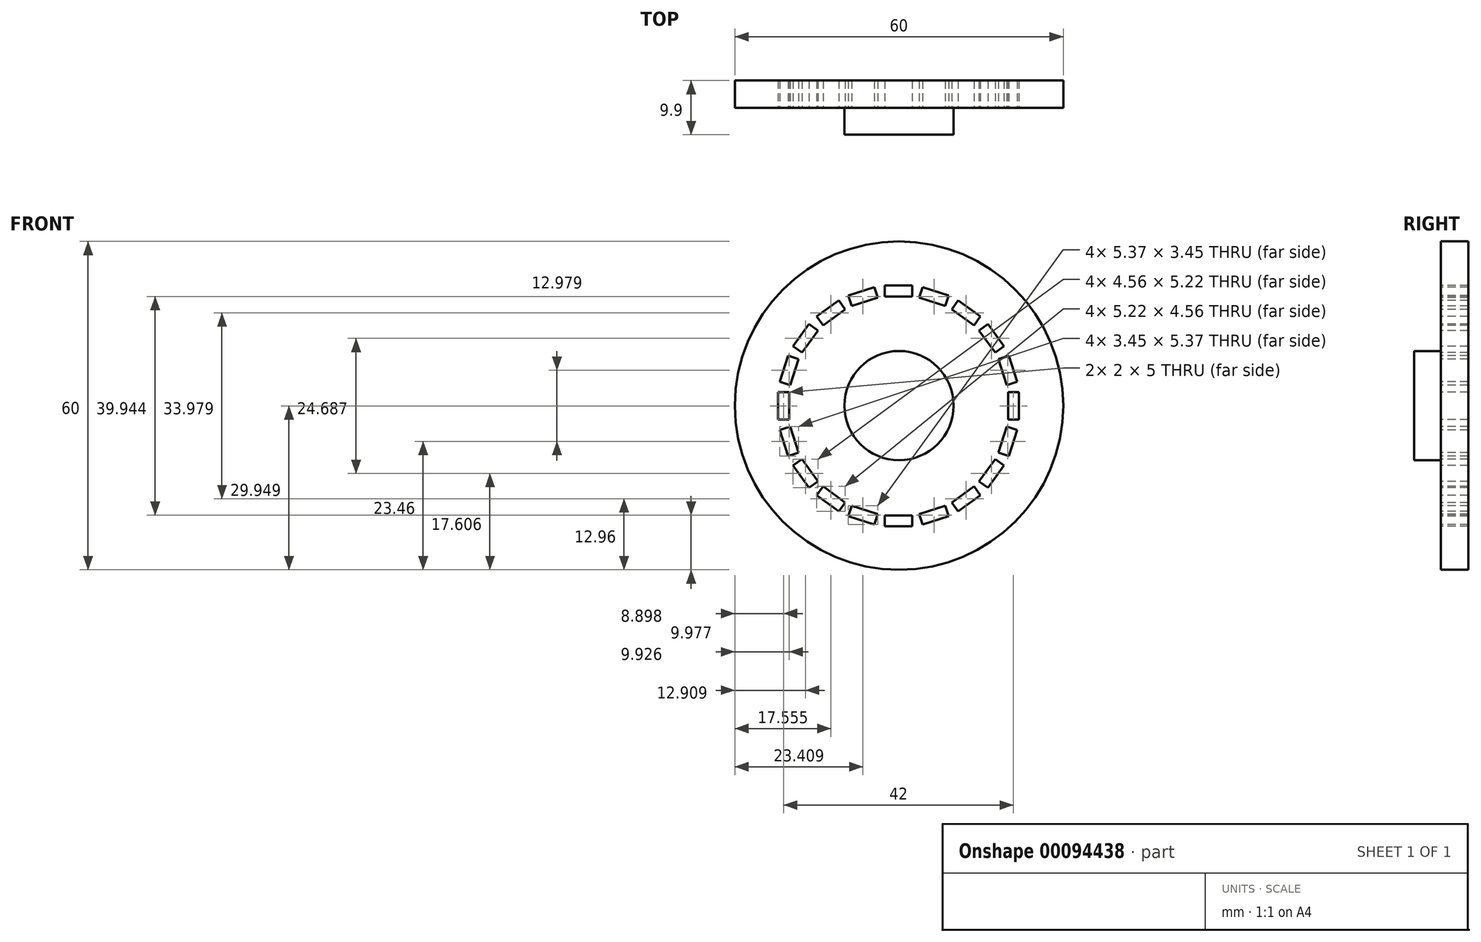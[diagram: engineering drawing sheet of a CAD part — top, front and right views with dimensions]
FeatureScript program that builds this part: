
annotation { "Feature Type Name" : "Feature", "Feature Type Description" : "" }
export const myFeature = defineFeature(function(context is Context, id is Id, definition is map)
    precondition{}
    {
        {
            var Q0;
            Q0=qCreatedBy(makeId("Front.planeOp"),FACE);
            var sketch = newSketch(context, id + "F0", { "sketchPlane" : qUnion([Q0])});
            skCircle(sketch, "E0", {"center": v(0, 0) * mm, "radius": 30 * mm});
            skSolve(sketch);
        }
        {
            var Q0;
            Q0=makeQuery(id+"F0.imprint","IMPRINT",FACE,{"disambiguationData":[TD([[makeQuery(id+"F0.imprint","IMPRINT",EDGE,{"derivedFrom":sQuery(id+"F0.wireOp",EDGE,"E0")}),1.0]])]});
            extrude(context, id + "F1", {"entities" : qUnion([Q0]), "depth" : 5 * mm});
        }
        {
            var Q0;
            Q0=makeQuery(id+"F1.opExtrude","CAP_FACE",FACE,{"disambiguationData":[OSD([sQuery(id+"F0.wireOp",EDGE,"E0")])],"isStart":false});
            var sketch = newSketch(context, id + "F2", { "sketchPlane" : qUnion([Q0])});
            skLineSegment(sketch, "E1", {"start": v(-2.6, 20.95) * mm, "end": v(-2.6, 21.95) * mm});
            skLineSegment(sketch, "E2", {"start": v(-2.6, 21.95) * mm, "end": v(2.4, 21.95) * mm});
            skLineSegment(sketch, "E3", {"start": v(2.4, 21.95) * mm, "end": v(2.4, 19.95) * mm});
            skLineSegment(sketch, "E4", {"start": v(2.4, 19.95) * mm, "end": v(-2.6, 19.95) * mm});
            skLineSegment(sketch, "E5", {"start": v(-2.6, 19.95) * mm, "end": v(-2.6, 20.95) * mm});
            skLineSegment(sketch, "E6.1.0", {"start": v(-9.28, 20.1) * mm, "end": v(-4.52, 21.64) * mm});
            skLineSegment(sketch, "E6.1.1", {"start": v(-3.9, 19.74) * mm, "end": v(-8.66, 18.2) * mm});
            skLineSegment(sketch, "E6.1.2", {"start": v(-8.66, 18.2) * mm, "end": v(-8.97, 19.15) * mm});
            skLineSegment(sketch, "E6.1.3", {"start": v(-8.97, 19.15) * mm, "end": v(-9.28, 20.1) * mm});
            skLineSegment(sketch, "E6.1.4", {"start": v(-4.52, 21.64) * mm, "end": v(-3.9, 19.74) * mm});
            skLineSegment(sketch, "E6.2.0", {"start": v(-15.06, 16.28) * mm, "end": v(-11.01, 19.22) * mm});
            skLineSegment(sketch, "E6.2.1", {"start": v(-9.83, 17.6) * mm, "end": v(-13.88, 14.66) * mm});
            skLineSegment(sketch, "E6.2.2", {"start": v(-13.88, 14.66) * mm, "end": v(-14.47, 15.47) * mm});
            skLineSegment(sketch, "E6.2.3", {"start": v(-14.47, 15.47) * mm, "end": v(-15.06, 16.28) * mm});
            skLineSegment(sketch, "E6.2.4", {"start": v(-11.01, 19.22) * mm, "end": v(-9.83, 17.6) * mm});
            skLineSegment(sketch, "E6.3.0", {"start": v(-19.37, 10.86) * mm, "end": v(-16.43, 14.9) * mm});
            skLineSegment(sketch, "E6.3.1", {"start": v(-14.81, 13.73) * mm, "end": v(-17.75, 9.68) * mm});
            skLineSegment(sketch, "E6.3.2", {"start": v(-17.75, 9.68) * mm, "end": v(-18.56, 10.27) * mm});
            skLineSegment(sketch, "E6.3.3", {"start": v(-18.56, 10.27) * mm, "end": v(-19.37, 10.86) * mm});
            skLineSegment(sketch, "E6.3.4", {"start": v(-16.43, 14.9) * mm, "end": v(-14.81, 13.73) * mm});
            skLineSegment(sketch, "E6.4.0", {"start": v(-21.8, 4.37) * mm, "end": v(-20.25, 9.13) * mm});
            skLineSegment(sketch, "E6.4.1", {"start": v(-18.35, 8.5) * mm, "end": v(-19.9, 3.75) * mm});
            skLineSegment(sketch, "E6.4.2", {"start": v(-19.9, 3.75) * mm, "end": v(-20.85, 4.06) * mm});
            skLineSegment(sketch, "E6.4.3", {"start": v(-20.85, 4.06) * mm, "end": v(-21.8, 4.37) * mm});
            skLineSegment(sketch, "E6.4.4", {"start": v(-20.25, 9.13) * mm, "end": v(-18.35, 8.5) * mm});
            skLineSegment(sketch, "E6.5.0", {"start": v(-22.1, -2.55) * mm, "end": v(-22.1, 2.45) * mm});
            skLineSegment(sketch, "E6.5.1", {"start": v(-20.1, 2.45) * mm, "end": v(-20.1, -2.55) * mm});
            skLineSegment(sketch, "E6.5.2", {"start": v(-20.1, -2.55) * mm, "end": v(-21.1, -2.55) * mm});
            skLineSegment(sketch, "E6.5.3", {"start": v(-21.1, -2.55) * mm, "end": v(-22.1, -2.55) * mm});
            skLineSegment(sketch, "E6.5.4", {"start": v(-22.1, 2.45) * mm, "end": v(-20.1, 2.45) * mm});
            skLineSegment(sketch, "E6.6.0", {"start": v(-20.25, -9.23) * mm, "end": v(-21.8, -4.47) * mm});
            skLineSegment(sketch, "E6.6.1", {"start": v(-19.9, -3.85) * mm, "end": v(-18.35, -8.6) * mm});
            skLineSegment(sketch, "E6.6.2", {"start": v(-18.35, -8.6) * mm, "end": v(-19.3, -8.92) * mm});
            skLineSegment(sketch, "E6.6.3", {"start": v(-19.3, -8.92) * mm, "end": v(-20.25, -9.23) * mm});
            skLineSegment(sketch, "E6.6.4", {"start": v(-21.8, -4.47) * mm, "end": v(-19.9, -3.85) * mm});
            skLineSegment(sketch, "E6.7.0", {"start": v(-16.43, -15) * mm, "end": v(-19.37, -10.96) * mm});
            skLineSegment(sketch, "E6.7.1", {"start": v(-17.75, -9.78) * mm, "end": v(-14.81, -13.83) * mm});
            skLineSegment(sketch, "E6.7.2", {"start": v(-14.81, -13.83) * mm, "end": v(-15.62, -14.42) * mm});
            skLineSegment(sketch, "E6.7.3", {"start": v(-15.62, -14.42) * mm, "end": v(-16.43, -15) * mm});
            skLineSegment(sketch, "E6.7.4", {"start": v(-19.37, -10.96) * mm, "end": v(-17.75, -9.78) * mm});
            skLineSegment(sketch, "E6.8.0", {"start": v(-11.01, -19.32) * mm, "end": v(-15.06, -16.38) * mm});
            skLineSegment(sketch, "E6.8.1", {"start": v(-13.88, -14.76) * mm, "end": v(-9.83, -17.7) * mm});
            skLineSegment(sketch, "E6.8.2", {"start": v(-9.83, -17.7) * mm, "end": v(-10.42, -18.5) * mm});
            skLineSegment(sketch, "E6.8.3", {"start": v(-10.42, -18.5) * mm, "end": v(-11.01, -19.32) * mm});
            skLineSegment(sketch, "E6.8.4", {"start": v(-15.06, -16.38) * mm, "end": v(-13.88, -14.76) * mm});
            skLineSegment(sketch, "E6.9.0", {"start": v(-4.52, -21.75) * mm, "end": v(-9.28, -20.2) * mm});
            skLineSegment(sketch, "E6.9.1", {"start": v(-8.66, -18.3) * mm, "end": v(-3.9, -19.84) * mm});
            skLineSegment(sketch, "E6.9.2", {"start": v(-3.9, -19.84) * mm, "end": v(-4.21, -20.8) * mm});
            skLineSegment(sketch, "E6.9.3", {"start": v(-4.21, -20.8) * mm, "end": v(-4.52, -21.75) * mm});
            skLineSegment(sketch, "E6.9.4", {"start": v(-9.28, -20.2) * mm, "end": v(-8.66, -18.3) * mm});
            skLineSegment(sketch, "E6.10.0", {"start": v(2.4, -22.05) * mm, "end": v(-2.6, -22.05) * mm});
            skLineSegment(sketch, "E6.10.1", {"start": v(-2.6, -20.05) * mm, "end": v(2.4, -20.05) * mm});
            skLineSegment(sketch, "E6.10.2", {"start": v(2.4, -20.05) * mm, "end": v(2.4, -21.05) * mm});
            skLineSegment(sketch, "E6.10.3", {"start": v(2.4, -21.05) * mm, "end": v(2.4, -22.05) * mm});
            skLineSegment(sketch, "E6.10.4", {"start": v(-2.6, -22.05) * mm, "end": v(-2.6, -20.05) * mm});
            skLineSegment(sketch, "E6.11.0", {"start": v(9.07, -20.2) * mm, "end": v(4.32, -21.75) * mm});
            skLineSegment(sketch, "E6.11.1", {"start": v(3.7, -19.84) * mm, "end": v(8.46, -18.3) * mm});
            skLineSegment(sketch, "E6.11.2", {"start": v(8.46, -18.3) * mm, "end": v(8.77, -19.25) * mm});
            skLineSegment(sketch, "E6.11.3", {"start": v(8.77, -19.25) * mm, "end": v(9.07, -20.2) * mm});
            skLineSegment(sketch, "E6.11.4", {"start": v(4.32, -21.75) * mm, "end": v(3.7, -19.84) * mm});
            skLineSegment(sketch, "E6.12.0", {"start": v(14.85, -16.38) * mm, "end": v(10.8, -19.32) * mm});
            skLineSegment(sketch, "E6.12.1", {"start": v(9.63, -17.7) * mm, "end": v(13.68, -14.76) * mm});
            skLineSegment(sketch, "E6.12.2", {"start": v(13.68, -14.76) * mm, "end": v(14.26, -15.57) * mm});
            skLineSegment(sketch, "E6.12.3", {"start": v(14.26, -15.57) * mm, "end": v(14.85, -16.38) * mm});
            skLineSegment(sketch, "E6.12.4", {"start": v(10.8, -19.32) * mm, "end": v(9.63, -17.7) * mm});
            skLineSegment(sketch, "E6.13.0", {"start": v(19.17, -10.96) * mm, "end": v(16.23, -15) * mm});
            skLineSegment(sketch, "E6.13.1", {"start": v(14.6, -13.83) * mm, "end": v(17.55, -9.78) * mm});
            skLineSegment(sketch, "E6.13.2", {"start": v(17.55, -9.78) * mm, "end": v(18.36, -10.37) * mm});
            skLineSegment(sketch, "E6.13.3", {"start": v(18.36, -10.37) * mm, "end": v(19.17, -10.96) * mm});
            skLineSegment(sketch, "E6.13.4", {"start": v(16.23, -15) * mm, "end": v(14.6, -13.83) * mm});
            skLineSegment(sketch, "E6.14.0", {"start": v(21.6, -4.47) * mm, "end": v(20.05, -9.23) * mm});
            skLineSegment(sketch, "E6.14.1", {"start": v(18.15, -8.6) * mm, "end": v(19.7, -3.85) * mm});
            skLineSegment(sketch, "E6.14.2", {"start": v(19.7, -3.85) * mm, "end": v(20.64, -4.16) * mm});
            skLineSegment(sketch, "E6.14.3", {"start": v(20.64, -4.16) * mm, "end": v(21.6, -4.47) * mm});
            skLineSegment(sketch, "E6.14.4", {"start": v(20.05, -9.23) * mm, "end": v(18.15, -8.6) * mm});
            skLineSegment(sketch, "E6.15.0", {"start": v(21.9, 2.45) * mm, "end": v(21.9, -2.55) * mm});
            skLineSegment(sketch, "E6.15.1", {"start": v(19.9, -2.55) * mm, "end": v(19.9, 2.45) * mm});
            skLineSegment(sketch, "E6.15.2", {"start": v(19.9, 2.45) * mm, "end": v(20.9, 2.45) * mm});
            skLineSegment(sketch, "E6.15.3", {"start": v(20.9, 2.45) * mm, "end": v(21.9, 2.45) * mm});
            skLineSegment(sketch, "E6.15.4", {"start": v(21.9, -2.55) * mm, "end": v(19.9, -2.55) * mm});
            skLineSegment(sketch, "E6.16.0", {"start": v(20.05, 9.13) * mm, "end": v(21.6, 4.37) * mm});
            skLineSegment(sketch, "E6.16.1", {"start": v(19.7, 3.75) * mm, "end": v(18.15, 8.5) * mm});
            skLineSegment(sketch, "E6.16.2", {"start": v(18.15, 8.5) * mm, "end": v(19.1, 8.82) * mm});
            skLineSegment(sketch, "E6.16.3", {"start": v(19.1, 8.82) * mm, "end": v(20.05, 9.13) * mm});
            skLineSegment(sketch, "E6.16.4", {"start": v(21.6, 4.37) * mm, "end": v(19.7, 3.75) * mm});
            skLineSegment(sketch, "E6.17.0", {"start": v(16.23, 14.9) * mm, "end": v(19.17, 10.86) * mm});
            skLineSegment(sketch, "E6.17.1", {"start": v(17.55, 9.68) * mm, "end": v(14.6, 13.73) * mm});
            skLineSegment(sketch, "E6.17.2", {"start": v(14.6, 13.73) * mm, "end": v(15.42, 14.32) * mm});
            skLineSegment(sketch, "E6.17.3", {"start": v(15.42, 14.32) * mm, "end": v(16.23, 14.9) * mm});
            skLineSegment(sketch, "E6.17.4", {"start": v(19.17, 10.86) * mm, "end": v(17.55, 9.68) * mm});
            skLineSegment(sketch, "E6.18.0", {"start": v(10.8, 19.22) * mm, "end": v(14.85, 16.28) * mm});
            skLineSegment(sketch, "E6.18.1", {"start": v(13.68, 14.66) * mm, "end": v(9.63, 17.6) * mm});
            skLineSegment(sketch, "E6.18.2", {"start": v(9.63, 17.6) * mm, "end": v(10.22, 18.4) * mm});
            skLineSegment(sketch, "E6.18.3", {"start": v(10.22, 18.4) * mm, "end": v(10.8, 19.22) * mm});
            skLineSegment(sketch, "E6.18.4", {"start": v(14.85, 16.28) * mm, "end": v(13.68, 14.66) * mm});
            skLineSegment(sketch, "E6.19.0", {"start": v(4.32, 21.64) * mm, "end": v(9.07, 20.1) * mm});
            skLineSegment(sketch, "E6.19.1", {"start": v(8.46, 18.2) * mm, "end": v(3.7, 19.74) * mm});
            skLineSegment(sketch, "E6.19.2", {"start": v(3.7, 19.74) * mm, "end": v(4.01, 20.7) * mm});
            skLineSegment(sketch, "E6.19.3", {"start": v(4.01, 20.7) * mm, "end": v(4.32, 21.64) * mm});
            skLineSegment(sketch, "E6.19.4", {"start": v(9.07, 20.1) * mm, "end": v(8.46, 18.2) * mm});
            skPoint(sketch, "E6.center", {"position": v(-0.1, -0.05) * mm});
            skSolve(sketch);
        }
        {
            var Q0;
            Q0 = qSketchRegion(id + "F2", true);
            extrude(context, id + "F3", {"entities" : qUnion([Q0]), "operationType" : NewBodyOperationType.REMOVE, "endBound" : BoundingType.THROUGH_ALL, "oppositeDirection" : true, "depth" : 25 * mm});
        }
        {
            var Q0;
            Q0=makeQuery(id+"F1.opExtrude","CAP_FACE",FACE,{"disambiguationData":[OSD([sQuery(id+"F0.wireOp",EDGE,"E0")])],"isStart":false});
            var sketch = newSketch(context, id + "F4", { "sketchPlane" : qUnion([Q0])});
            skCircle(sketch, "E7", {"center": v(0, 0) * mm, "radius": 9.97 * mm});
            skSolve(sketch);
        }
        {
            var Q0;
            Q0 = qSketchRegion(id + "F4", true);
            extrude(context, id + "F5", {"entities" : qUnion([Q0]), "operationType" : NewBodyOperationType.ADD, "depth" : 4.9 * mm});
        }
    });
